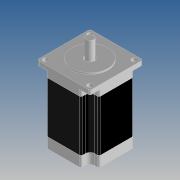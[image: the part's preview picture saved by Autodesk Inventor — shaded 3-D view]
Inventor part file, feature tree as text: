
AUTODESK INVENTOR PART (.ipt)
format: ipt  version: 2017 (Build 210142000, 142)  size: 272,384 bytes
history: native  units: mm
features: other x6, sketch x5, extrude x4, plane x2, split x2, fillet x1, revolve x1
ambient origin geometry x8: Origin, YZ Plane, XZ Plane, XY Plane, X Axis, Y Axis, Z Axis, Center Point
bodies: Body1 (feature_tree), Body2 (feature_tree), Body3 (feature_tree), Body4 (feature_tree)
feature tree (21):
  other  "Sólido1"
  extrude  "Extrusión1"  Depth=2.0mm
  extrude  "Extrusión2"  Depth=61.0mm
  extrude  "Extrusión3"  Depth=4.7mm TaperAngle=0.0deg
  fillet  "Empalme1"  Radius=37.0mm
  plane  "Plano de trabajo1"
  plane  "Plano de trabajo2"
  split  "Dividir1"
  split  "Dividir2"
  revolve  "Revolución1"  [1 undecoded]
  extrude  "Extrusión4"  [1 undecoded]
  sketch  "Boceto1"  dims[d0=56.0mm d1=2.0mm]
  sketch  "Boceto2"  dims[d2=5.3mm d3=61.0mm]
  sketch  "Boceto3"  dims[d4=10.0mm d5=4.7mm d6=0.0mm d7=37.0mm]
  sketch  "Boceto4"  dims[d8=71.3mm d9=0.0mm d10=38.0mm]
  other  "Sólido6"
  sketch  "Boceto5"  dims[d11=1.6mm d12=0.0mm d13=-11.0mm d14=-11.0mm d15=2.0mm d16=8.0mm d17=19.0mm d18=90.0deg d19=7.4mm d20=2.0mm d21=10.0mm d22=0.0mm]
  other  "Sólido2"
  other  "Sólido3"
  other  "Sólido4"
  other  "Sólido5"
note: 2 required parameter values undecoded (feature->parameter linkage not recoverable at this tier; creation-order binding heuristic only, values carry confidence <= 0.55)